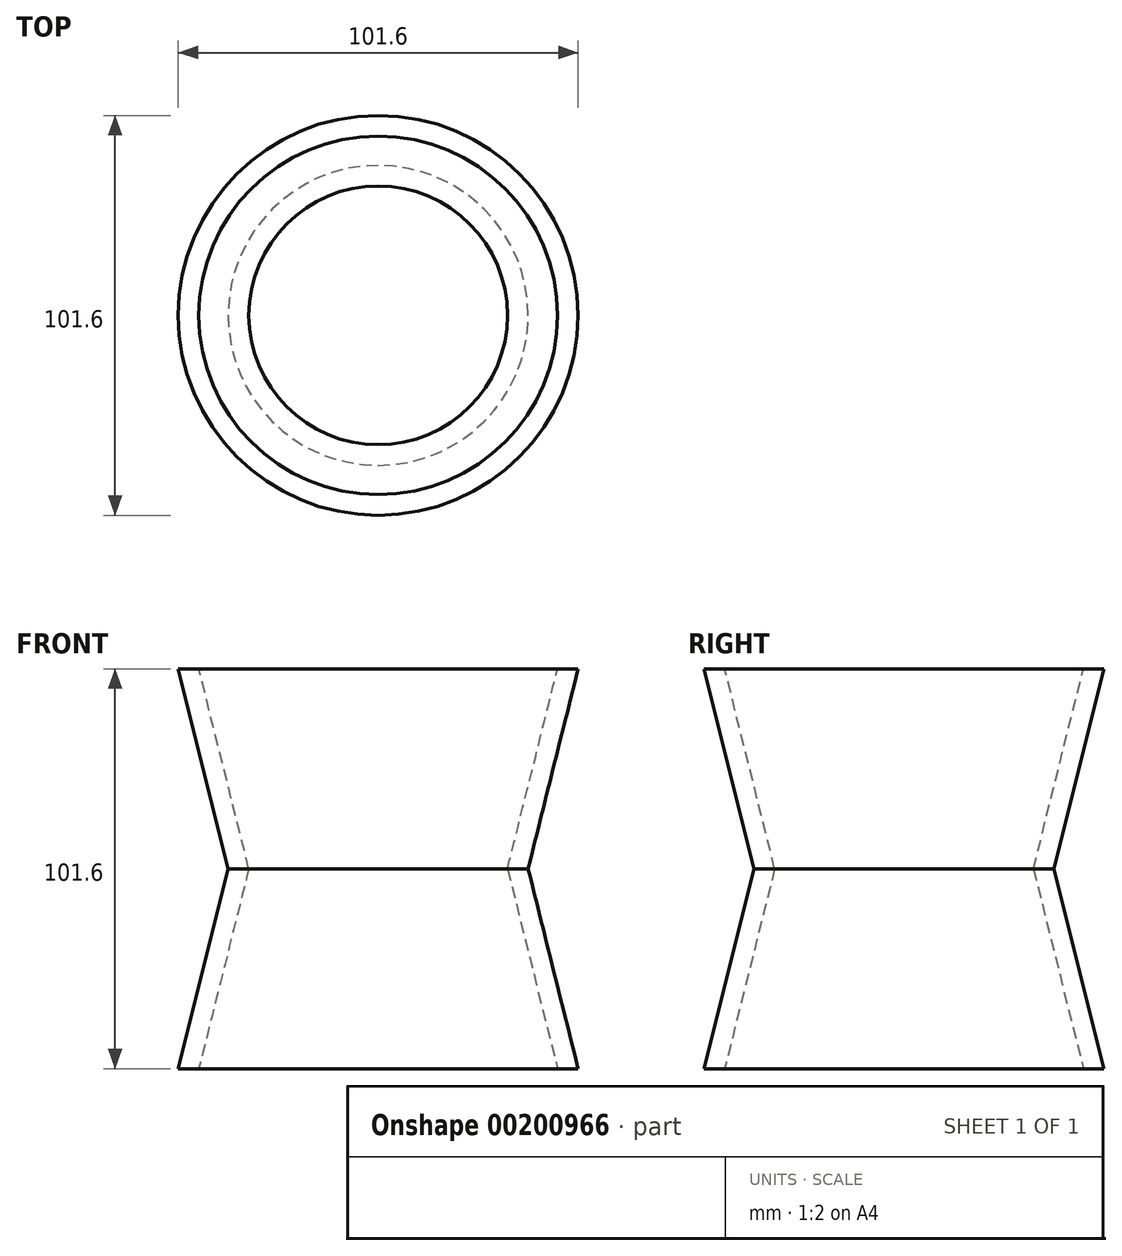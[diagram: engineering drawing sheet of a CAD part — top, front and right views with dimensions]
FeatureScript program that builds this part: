
annotation { "Feature Type Name" : "Feature", "Feature Type Description" : "" }
export const myFeature = defineFeature(function(context is Context, id is Id, definition is map)
    precondition{}
    {
        {
            var Q0;
            Q0=qCreatedBy(makeId("Top.planeOp"),FACE);
            var sketch = newSketch(context, id + "F0", { "sketchPlane" : qUnion([Q0])});
            skCircle(sketch, "E0", {"center": v(0, 0) * mm, "radius": 38.1 * mm});
            skSolve(sketch);
        }
        {
            var Q0;
            Q0=makeQuery(id+"F0.imprint","IMPRINT",FACE,{"disambiguationData":[TD([[makeQuery(id+"F0.imprint","IMPRINT",EDGE,{"derivedFrom":sQuery(id+"F0.wireOp",EDGE,"E0")}),1.0]])]});
            cPlane(context, id + "F1", {"entities" : qUnion([Q0]), "cplaneType" : CPlaneType.OFFSET, "offset" : 50.8 * mm, "width" : 152.4 * mm, "height" : 152.4 * mm});
        }
        {
            var Q0;
            Q0=qCreatedBy(id+"F1.planeOp",FACE);
            var sketch = newSketch(context, id + "F2", { "sketchPlane" : qUnion([Q0])});
            skCircle(sketch, "E1", {"center": v(0, 0) * mm, "radius": 50.8 * mm});
            skSolve(sketch);
        }
        {
            var Q0;
            Q0=makeQuery(id+"F2.imprint","IMPRINT",FACE,{"disambiguationData":[TD([[makeQuery(id+"F2.imprint","IMPRINT",EDGE,{"derivedFrom":sQuery(id+"F2.wireOp",EDGE,"E1")}),1.0]])]});
            var Q1;
            Q1=makeQuery(id+"F0.imprint","IMPRINT",FACE,{"disambiguationData":[TD([[makeQuery(id+"F0.imprint","IMPRINT",EDGE,{"derivedFrom":sQuery(id+"F0.wireOp",EDGE,"E0")}),1.0]])]});
            loft(context, id + "F3", {"sheetProfilesArray" : [{ "sheetProfileEntities" : qUnion([Q0]) }, { "sheetProfileEntities" : qUnion([Q1]) }]});
        }
        {
            var Q0;
            Q0=makeQuery(id+"F3.opLoft","SWEPT_BODY",BODY,{"disambiguationData":[OSD([makeQuery(id+"F0.imprint","IMPRINT",FACE,{"disambiguationData":[TD([[makeQuery(id+"F0.imprint","IMPRINT",EDGE,{"derivedFrom":sQuery(id+"F0.wireOp",EDGE,"E0")}),1.0]])]}),makeQuery(id+"F2.imprint","IMPRINT",FACE,{"disambiguationData":[TD([[makeQuery(id+"F2.imprint","IMPRINT",EDGE,{"derivedFrom":sQuery(id+"F2.wireOp",EDGE,"E1")}),1.0]])]})])]});
            var Q1;
            Q1=qCreatedBy(makeId("Top.planeOp"),FACE);
            mirror(context, id + "F4", {"operationType" : NewBodyOperationType.ADD, "entities" : qUnion([Q0]), "mirrorPlane" : qUnion([Q1])});
        }
        {
            var Q0;
            Q0=makeQuery(id+"F4.opPattern","COPY",FACE,{"derivedFrom":makeQuery(id+"F3.opLoft","CAP_FACE",FACE,{"disambiguationData":[OSD([makeQuery(id+"F2.imprint","IMPRINT",FACE,{"disambiguationData":[TD([[makeQuery(id+"F2.imprint","IMPRINT",EDGE,{"derivedFrom":sQuery(id+"F2.wireOp",EDGE,"E1")}),1.0]])]})])],"isStart":true}),"instanceName":"1"});
            var Q1;
            Q1=makeQuery(id+"F3.opLoft","CAP_FACE",FACE,{"disambiguationData":[OSD([makeQuery(id+"F2.imprint","IMPRINT",FACE,{"disambiguationData":[TD([[makeQuery(id+"F2.imprint","IMPRINT",EDGE,{"derivedFrom":sQuery(id+"F2.wireOp",EDGE,"E1")}),1.0]])]})])],"isStart":true});
            shell(context, id + "F5", {"entities" : qUnion([Q0, Q1]), "thickness" : 5.08 * mm});
        }
    });
